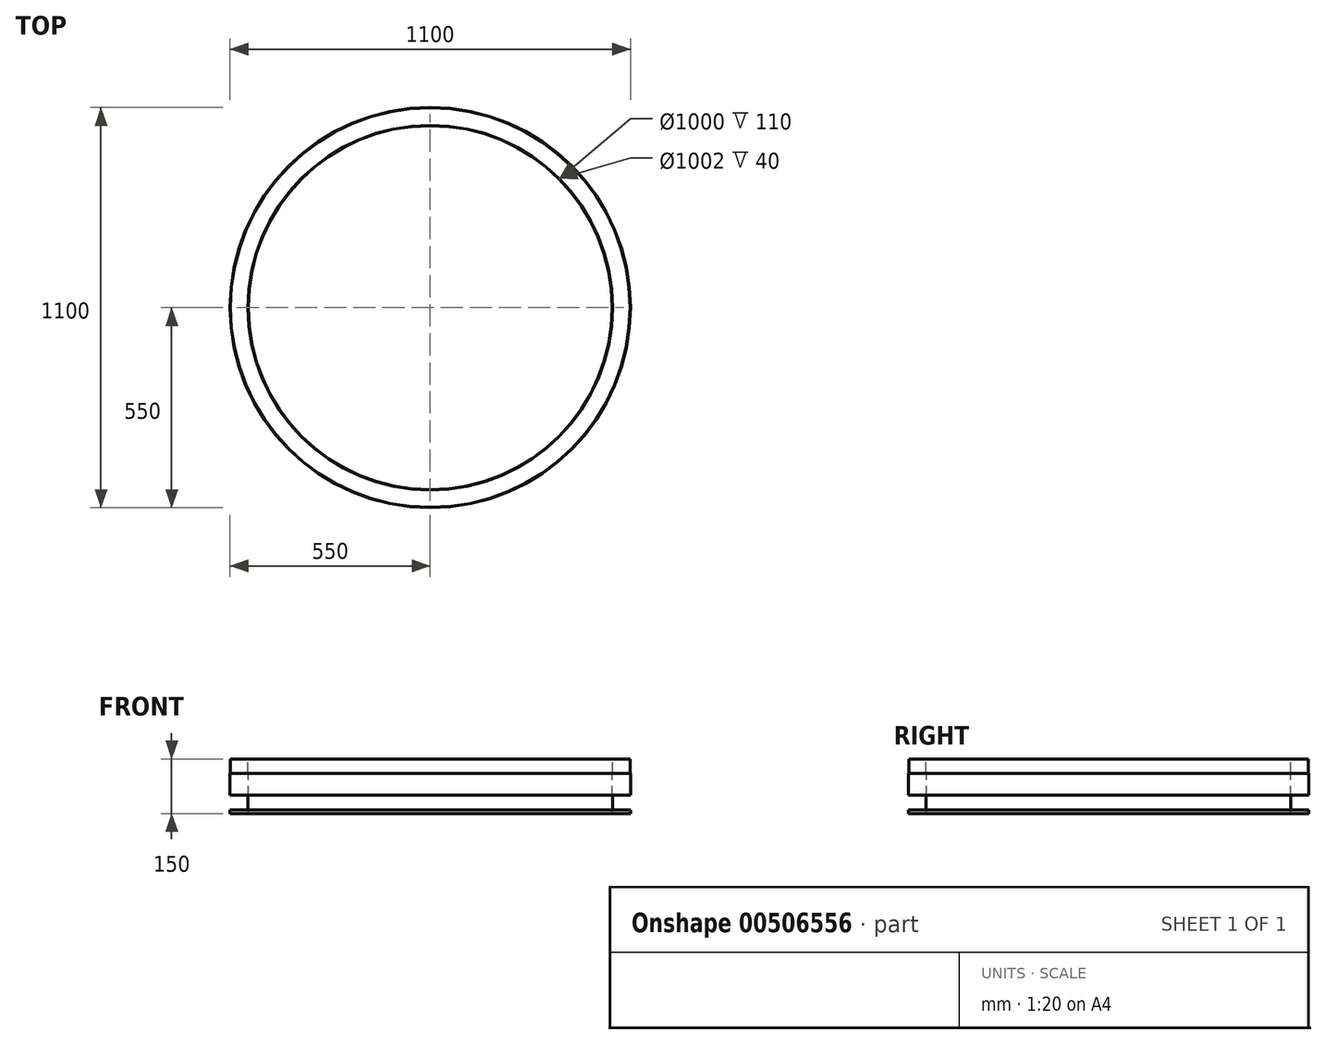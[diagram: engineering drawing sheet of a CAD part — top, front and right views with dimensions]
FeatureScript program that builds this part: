
annotation { "Feature Type Name" : "Feature", "Feature Type Description" : "" }
export const myFeature = defineFeature(function(context is Context, id is Id, definition is map)
    precondition{}
    {
        {
            var Q0;
            Q0=qCreatedBy(makeId("Front.planeOp"),FACE);
            var sketch = newSketch(context, id + "F0", { "sketchPlane" : qUnion([Q0])});
            skLineSegment(sketch, "E0", {"start": v(0, 710.75) * mm, "end": v(0, -704.58) * mm, "construction": true});
            skLineSegment(sketch, "E1", {"start": v(-500, 300.65) * mm, "end": v(-500, 410.65) * mm});
            skLineSegment(sketch, "E2", {"start": v(-500, 410.65) * mm, "end": v(-501, 410.65) * mm});
            skLineSegment(sketch, "E3", {"start": v(-501, 410.65) * mm, "end": v(-501, 450.65) * mm});
            skLineSegment(sketch, "E4", {"start": v(-501, 450.65) * mm, "end": v(-549, 450.65) * mm});
            skLineSegment(sketch, "E5", {"start": v(-549, 450.65) * mm, "end": v(-549, 410.65) * mm});
            skLineSegment(sketch, "E6", {"start": v(-549, 410.65) * mm, "end": v(-550, 410.65) * mm});
            skLineSegment(sketch, "E7", {"start": v(-550, 410.65) * mm, "end": v(-550, 350.65) * mm});
            skLineSegment(sketch, "E8", {"start": v(-550, 350.65) * mm, "end": v(-501, 350.65) * mm});
            skLineSegment(sketch, "E9", {"start": v(-501, 350.65) * mm, "end": v(-501, 310.65) * mm});
            skLineSegment(sketch, "E10", {"start": v(-501, 310.65) * mm, "end": v(-550, 310.65) * mm});
            skLineSegment(sketch, "E11", {"start": v(-550, 310.65) * mm, "end": v(-550, 300.65) * mm});
            skLineSegment(sketch, "E12", {"start": v(-550, 300.65) * mm, "end": v(-500, 300.65) * mm});
            skSolve(sketch);
        }
        {
            var Q0;
            Q0=qSketchRegion(id+"F0",true);
            var Q1;
            Q1=sQuery(id+"F0.wireOp",EDGE,"E0");
            revolve(context, id + "F1", {"entities" : qUnion([Q0]), "axis" : qUnion([Q1]), "revolveType" : RevolveType.FULL});
        }
    });
